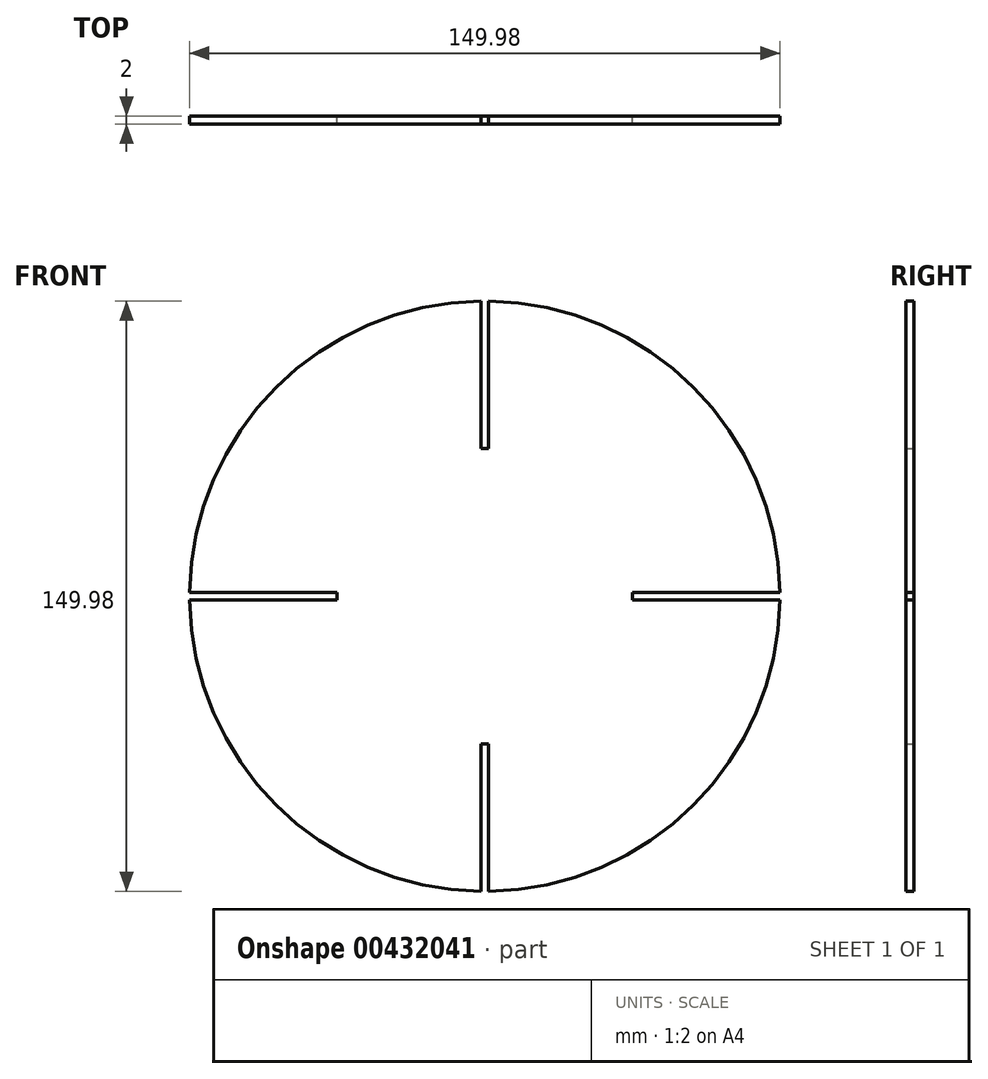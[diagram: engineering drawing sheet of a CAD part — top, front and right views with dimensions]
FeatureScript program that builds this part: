
annotation { "Feature Type Name" : "Feature", "Feature Type Description" : "" }
export const myFeature = defineFeature(function(context is Context, id is Id, definition is map)
    precondition{}
    {
        {
            var Q0;
            Q0=qCreatedBy(makeId("Front.planeOp"),FACE);
            var sketch = newSketch(context, id + "F0", { "sketchPlane" : qUnion([Q0])});
            skArc(sketch, "E0", {"start": v(-1, 75) * mm, "mid": v(-53.03, 53.03) * mm, "end": v(-75, 1) * mm});
            skLineSegment(sketch, "E1.MirrorCS", {"start": v(-1, 75) * mm, "end": v(-1, 37.5) * mm});
            skLineSegment(sketch, "E2", {"start": v(-1, 37.5) * mm, "end": v(1, 37.5) * mm});
            skLineSegment(sketch, "E3.top", {"start": v(-75, 1) * mm, "end": v(-37.5, 1) * mm});
            skLineSegment(sketch, "E3.right", {"start": v(-37.5, 0) * mm, "end": v(-37.5, 1) * mm});
            skPoint(sketch, "E4.trimOffspring.start.orphan", {"position": v(-75, 0) * mm});
            skLineSegment(sketch, "E5.MirrorCS", {"start": v(37.5, 0) * mm, "end": v(37.5, 1) * mm});
            skLineSegment(sketch, "E6.MirrorCS", {"start": v(1, 37.5) * mm, "end": v(-1, 37.5) * mm});
            skArc(sketch, "E7.MirrorCS", {"start": v(1, 75) * mm, "mid": v(53.03, 53.03) * mm, "end": v(75, 1) * mm});
            skLineSegment(sketch, "E8.MirrorCS", {"start": v(75, 1) * mm, "end": v(37.5, 1) * mm});
            skPoint(sketch, "E9.MirrorP", {"position": v(75, 0) * mm});
            skLineSegment(sketch, "E10.MirrorCS", {"start": v(1, 75) * mm, "end": v(1, 37.5) * mm});
            skLineSegment(sketch, "E11.MirrorCS", {"start": v(-1, -37.5) * mm, "end": v(1, -37.5) * mm});
            skLineSegment(sketch, "E12.MirrorCS", {"start": v(1, -37.5) * mm, "end": v(-1, -37.5) * mm});
            skLineSegment(sketch, "E13.MirrorCS", {"start": v(37.5, 0) * mm, "end": v(37.5, -1) * mm});
            skLineSegment(sketch, "E14.MirrorCS", {"start": v(-37.5, 0) * mm, "end": v(-37.5, -1) * mm});
            skLineSegment(sketch, "E15.MirrorCS", {"start": v(-75, -1) * mm, "end": v(-37.5, -1) * mm});
            skLineSegment(sketch, "E16.MirrorCS", {"start": v(75, -1) * mm, "end": v(37.5, -1) * mm});
            skLineSegment(sketch, "E17.MirrorCS", {"start": v(1, -75) * mm, "end": v(1, -37.5) * mm});
            skArc(sketch, "E18.MirrorCS", {"start": v(1, -75) * mm, "mid": v(53.03, -53.03) * mm, "end": v(75, -1) * mm});
            skLineSegment(sketch, "E19.MirrorCS", {"start": v(-1, -75) * mm, "end": v(-1, -37.5) * mm});
            skArc(sketch, "E20.MirrorCS", {"start": v(-1, -75) * mm, "mid": v(-53.03, -53.03) * mm, "end": v(-75, -1) * mm});
            skPoint(sketch, "E21.MirrorCS.end.orphan", {"position": v(0, 37.5) * mm});
            skPoint(sketch, "E22.MirrorCS.end.orphan", {"position": v(0, -37.5) * mm});
            skSolve(sketch);
        }
        {
            var Q0;
            {var subQ6=sQuery(id+"F0.wireOp",EDGE,"E0");Q0=makeQuery(id+"F0.imprint","IMPRINT",FACE,{"disambiguationData":[TD([[makeQuery(id+"F0.imprint","IMPRINT",EDGE,{"derivedFrom":subQ6}),1.0]])]});}
            extrude(context, id + "F1", {"entities" : qUnion([Q0]), "depth" : 2 * mm});
        }
    });
